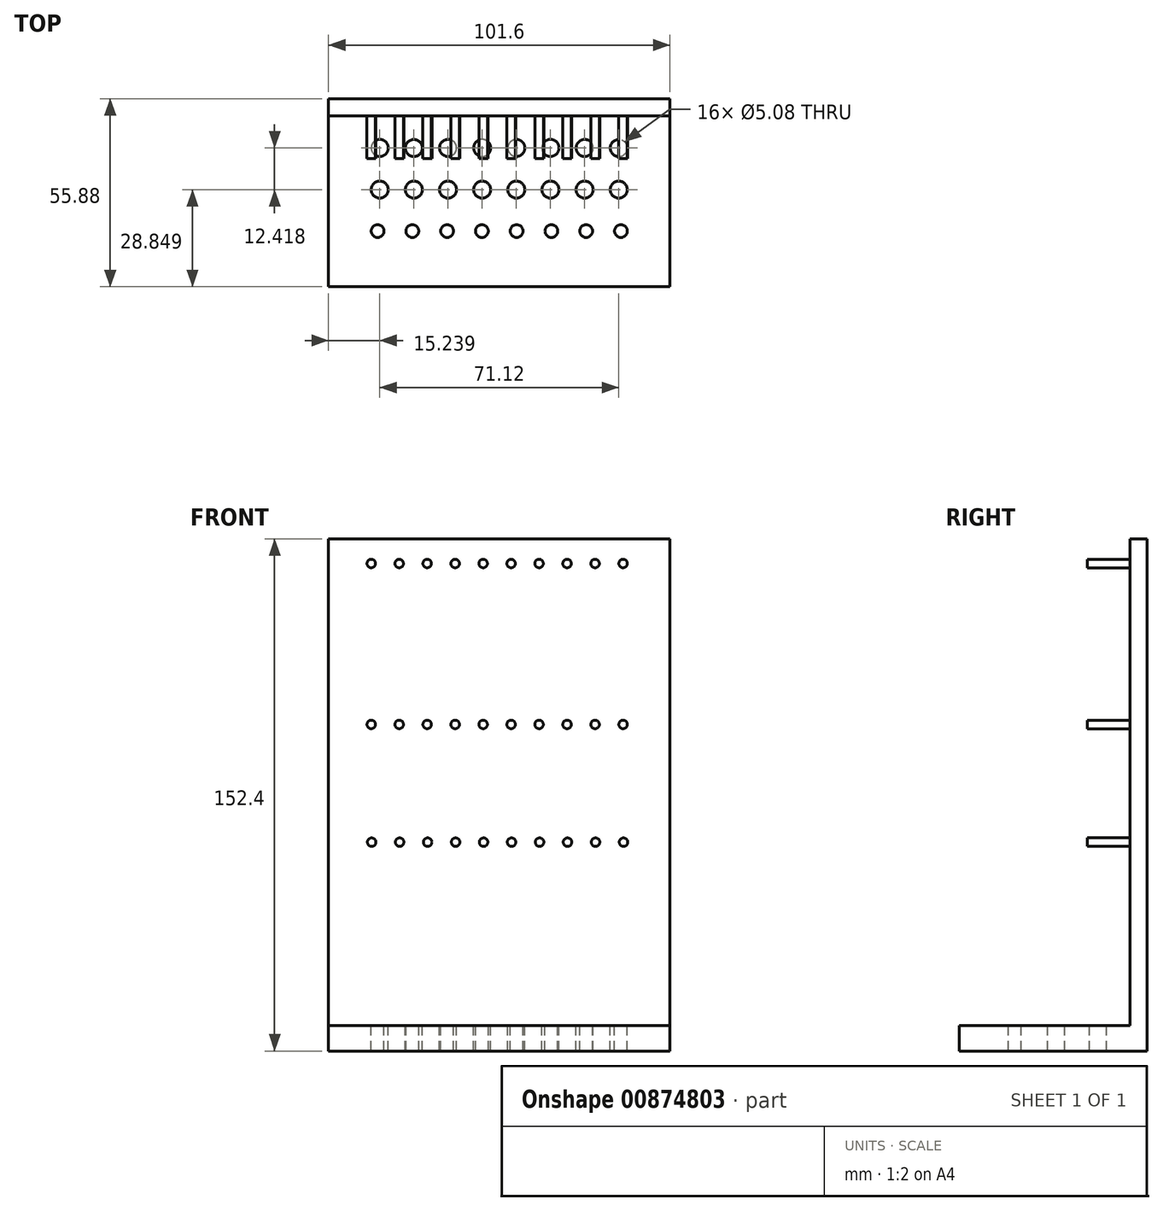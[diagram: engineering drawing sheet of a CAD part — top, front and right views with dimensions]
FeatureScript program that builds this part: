
annotation { "Feature Type Name" : "Feature", "Feature Type Description" : "" }
export const myFeature = defineFeature(function(context is Context, id is Id, definition is map)
    precondition{}
    {
        {
            var Q0;
            Q0=qCreatedBy(makeId("Front.planeOp"),FACE);
            var sketch = newSketch(context, id + "F0", { "sketchPlane" : qUnion([Q0])});
            skLineSegment(sketch, "E0", {"start": v(-60.63, 101.31) * mm, "end": v(40.97, 101.31) * mm});
            skLineSegment(sketch, "E1", {"start": v(40.97, 101.31) * mm, "end": v(40.97, -51.09) * mm});
            skLineSegment(sketch, "E2", {"start": v(40.97, -51.09) * mm, "end": v(-60.63, -51.09) * mm});
            skLineSegment(sketch, "E3", {"start": v(-60.63, -51.09) * mm, "end": v(-60.63, 101.31) * mm});
            skSolve(sketch);
        }
        {
            var Q0;
            Q0 = qSketchRegion(id + "F0", true);
            extrude(context, id + "F1", {"entities" : qUnion([Q0]), "depth" : 5.08 * mm, "offsetDistance" : 25.4 * mm});
        }
        {
            var Q0;
            Q0=makeQuery(id+"F1.opExtrude","CAP_FACE",FACE,{"disambiguationData":[OSD([sQuery(id+"F0.wireOp",EDGE,"E0"),sQuery(id+"F0.wireOp",EDGE,"E1"),sQuery(id+"F0.wireOp",EDGE,"E2"),sQuery(id+"F0.wireOp",EDGE,"E3")])],"isStart":false});
            var sketch = newSketch(context, id + "F2", { "sketchPlane" : qUnion([Q0])});
            skLineSegment(sketch, "E4", {"start": v(-60.63, -51.09) * mm, "end": v(40.97, -51.09) * mm});
            skLineSegment(sketch, "E5", {"start": v(40.97, -51.09) * mm, "end": v(40.97, -43.47) * mm});
            skLineSegment(sketch, "E6", {"start": v(40.97, -43.47) * mm, "end": v(-60.63, -43.47) * mm});
            skLineSegment(sketch, "E7", {"start": v(-60.63, -43.47) * mm, "end": v(-60.63, -51.09) * mm});
            skSolve(sketch);
        }
        {
            var Q0;
            Q0 = qSketchRegion(id + "F2", true);
            extrude(context, id + "F3", {"entities" : qUnion([Q0]), "operationType" : NewBodyOperationType.ADD, "depth" : 50.8 * mm, "offsetDistance" : 25.4 * mm});
        }
        {
            var Q0;
            Q0=makeQuery(id+"F3.opExtrude","SWEPT_FACE",FACE,{"disambiguationData":[OSD([sQuery(id+"F2.wireOp",EDGE,"E6")])]});
            var sketch = newSketch(context, id + "F4", { "sketchPlane" : qUnion([Q0])});
            skCircle(sketch, "E8", {"center": v(-45.4, -14.61) * mm, "radius": 2.54 * mm});
            skCircle(sketch, "E9.1.0.0", {"center": v(-35.23, -14.61) * mm, "radius": 2.54 * mm});
            skCircle(sketch, "E9.2.0.0", {"center": v(-25.07, -14.61) * mm, "radius": 2.54 * mm});
            skCircle(sketch, "E9.3.0.0", {"center": v(-14.91, -14.61) * mm, "radius": 2.54 * mm});
            skCircle(sketch, "E9.4.0.0", {"center": v(-4.75, -14.61) * mm, "radius": 2.54 * mm});
            skCircle(sketch, "E9.5.0.0", {"center": v(5.4, -14.61) * mm, "radius": 2.54 * mm});
            skCircle(sketch, "E9.6.0.0", {"center": v(15.57, -14.61) * mm, "radius": 2.54 * mm});
            skCircle(sketch, "E9.7.0.0", {"center": v(25.73, -14.61) * mm, "radius": 2.54 * mm});
            skLineSegment(sketch, "E9.direction1", {"start": v(-45.4, -14.61) * mm, "end": v(-35.23, -14.61) * mm, "construction": true});
            skSolve(sketch);
        }
        {
            var Q0;
            Q0 = qSketchRegion(id + "F4", true);
            extrude(context, id + "F5", {"entities" : qUnion([Q0]), "operationType" : NewBodyOperationType.REMOVE, "oppositeDirection" : true, "depth" : 25.4 * mm, "offsetDistance" : 25.4 * mm});
        }
        {
            var Q0;
            Q0=makeQuery(id+"F3.opExtrude","SWEPT_FACE",FACE,{"disambiguationData":[OSD([sQuery(id+"F2.wireOp",EDGE,"E6")])]});
            var sketch = newSketch(context, id + "F6", { "sketchPlane" : qUnion([Q0])});
            skCircle(sketch, "E10", {"center": v(-45.4, -27.03) * mm, "radius": 2.54 * mm});
            skCircle(sketch, "E11.1.0.0", {"center": v(-35.23, -27.03) * mm, "radius": 2.54 * mm});
            skCircle(sketch, "E11.2.0.0", {"center": v(-25.07, -27.03) * mm, "radius": 2.54 * mm});
            skCircle(sketch, "E11.3.0.0", {"center": v(-14.91, -27.03) * mm, "radius": 2.54 * mm});
            skCircle(sketch, "E11.4.0.0", {"center": v(-4.75, -27.03) * mm, "radius": 2.54 * mm});
            skCircle(sketch, "E11.5.0.0", {"center": v(5.4, -27.03) * mm, "radius": 2.54 * mm});
            skCircle(sketch, "E11.6.0.0", {"center": v(15.57, -27.03) * mm, "radius": 2.54 * mm});
            skCircle(sketch, "E11.7.0.0", {"center": v(25.73, -27.03) * mm, "radius": 2.54 * mm});
            skLineSegment(sketch, "E11.direction1", {"start": v(-45.4, -27.03) * mm, "end": v(-35.23, -27.03) * mm, "construction": true});
            skSolve(sketch);
        }
        {
            var Q0;
            Q0 = qSketchRegion(id + "F6", true);
            extrude(context, id + "F7", {"entities" : qUnion([Q0]), "operationType" : NewBodyOperationType.REMOVE, "oppositeDirection" : true, "depth" : 25.4 * mm, "offsetDistance" : 25.4 * mm});
        }
        {
            var Q0;
            Q0=makeQuery(id+"F3.opExtrude","SWEPT_FACE",FACE,{"disambiguationData":[OSD([sQuery(id+"F2.wireOp",EDGE,"E6")])]});
            var sketch = newSketch(context, id + "F8", { "sketchPlane" : qUnion([Q0])});
            skCircle(sketch, "E12", {"center": v(-46.03, -39.35) * mm, "radius": 1.9 * mm});
            skCircle(sketch, "E13.1.0.0", {"center": v(-35.68, -39.35) * mm, "radius": 1.9 * mm});
            skCircle(sketch, "E13.2.0.0", {"center": v(-25.34, -39.35) * mm, "radius": 1.9 * mm});
            skCircle(sketch, "E13.3.0.0", {"center": v(-15, -39.35) * mm, "radius": 1.9 * mm});
            skCircle(sketch, "E13.4.0.0", {"center": v(-4.66, -39.35) * mm, "radius": 1.9 * mm});
            skCircle(sketch, "E13.5.0.0", {"center": v(5.68, -39.35) * mm, "radius": 1.9 * mm});
            skCircle(sketch, "E13.6.0.0", {"center": v(16.02, -39.35) * mm, "radius": 1.9 * mm});
            skCircle(sketch, "E13.7.0.0", {"center": v(26.36, -39.35) * mm, "radius": 1.9 * mm});
            skLineSegment(sketch, "E13.direction1", {"start": v(-46.03, -39.35) * mm, "end": v(-35.68, -39.35) * mm, "construction": true});
            skSolve(sketch);
        }
        {
            var Q0;
            Q0=makeQuery(id+"F8.imprint","IMPRINT",FACE,{"disambiguationData":[TD([[makeQuery(id+"F8.imprint","IMPRINT",EDGE,{"derivedFrom":sQuery(id+"F8.wireOp",EDGE,"E13.7.0.0")}),1.0]])]});
            var Q1;
            Q1=makeQuery(id+"F8.imprint","IMPRINT",FACE,{"disambiguationData":[TD([[makeQuery(id+"F8.imprint","IMPRINT",EDGE,{"derivedFrom":sQuery(id+"F8.wireOp",EDGE,"E13.6.0.0")}),1.0]])]});
            var Q2;
            Q2=makeQuery(id+"F8.imprint","IMPRINT",FACE,{"disambiguationData":[TD([[makeQuery(id+"F8.imprint","IMPRINT",EDGE,{"derivedFrom":sQuery(id+"F8.wireOp",EDGE,"E13.5.0.0")}),1.0]])]});
            var Q3;
            Q3=makeQuery(id+"F8.imprint","IMPRINT",FACE,{"disambiguationData":[TD([[makeQuery(id+"F8.imprint","IMPRINT",EDGE,{"derivedFrom":sQuery(id+"F8.wireOp",EDGE,"E13.4.0.0")}),1.0]])]});
            var Q4;
            Q4=makeQuery(id+"F8.imprint","IMPRINT",FACE,{"disambiguationData":[TD([[makeQuery(id+"F8.imprint","IMPRINT",EDGE,{"derivedFrom":sQuery(id+"F8.wireOp",EDGE,"E13.3.0.0")}),1.0]])]});
            var Q5;
            Q5=makeQuery(id+"F8.imprint","IMPRINT",FACE,{"disambiguationData":[TD([[makeQuery(id+"F8.imprint","IMPRINT",EDGE,{"derivedFrom":sQuery(id+"F8.wireOp",EDGE,"E13.2.0.0")}),1.0]])]});
            var Q6;
            Q6=makeQuery(id+"F8.imprint","IMPRINT",FACE,{"disambiguationData":[TD([[makeQuery(id+"F8.imprint","IMPRINT",EDGE,{"derivedFrom":sQuery(id+"F8.wireOp",EDGE,"E13.1.0.0")}),1.0]])]});
            var Q7;
            Q7=makeQuery(id+"F8.imprint","IMPRINT",FACE,{"disambiguationData":[TD([[makeQuery(id+"F8.imprint","IMPRINT",EDGE,{"derivedFrom":sQuery(id+"F8.wireOp",EDGE,"E12")}),1.0]])]});
            extrude(context, id + "F9", {"entities" : qUnion([Q0, Q1, Q2, Q3, Q4, Q5, Q6, Q7]), "operationType" : NewBodyOperationType.REMOVE, "oppositeDirection" : true, "depth" : 25.4 * mm, "offsetDistance" : 25.4 * mm});
        }
        {
            var Q0;
            Q0=makeQuery(id+"F1.opExtrude","CAP_FACE",FACE,{"disambiguationData":[OSD([sQuery(id+"F0.wireOp",EDGE,"E0"),sQuery(id+"F0.wireOp",EDGE,"E1"),sQuery(id+"F0.wireOp",EDGE,"E2"),sQuery(id+"F0.wireOp",EDGE,"E3")])],"isStart":false});
            var sketch = newSketch(context, id + "F10", { "sketchPlane" : qUnion([Q0])});
            skCircle(sketch, "E14", {"center": v(-47.93, 93.94) * mm, "radius": 1.27 * mm});
            skCircle(sketch, "E15.1.0.0", {"center": v(-39.6, 93.94) * mm, "radius": 1.27 * mm});
            skCircle(sketch, "E15.2.0.0", {"center": v(-31.28, 93.94) * mm, "radius": 1.27 * mm});
            skCircle(sketch, "E15.3.0.0", {"center": v(-22.95, 93.94) * mm, "radius": 1.27 * mm});
            skCircle(sketch, "E15.4.0.0", {"center": v(-14.63, 93.94) * mm, "radius": 1.27 * mm});
            skCircle(sketch, "E15.5.0.0", {"center": v(-6.3, 93.94) * mm, "radius": 1.27 * mm});
            skCircle(sketch, "E15.6.0.0", {"center": v(2.02, 93.94) * mm, "radius": 1.27 * mm});
            skCircle(sketch, "E15.7.0.0", {"center": v(10.35, 93.94) * mm, "radius": 1.27 * mm});
            skCircle(sketch, "E15.8.0.0", {"center": v(18.67, 93.94) * mm, "radius": 1.27 * mm});
            skCircle(sketch, "E15.9.0.0", {"center": v(27, 93.94) * mm, "radius": 1.27 * mm});
            skLineSegment(sketch, "E15.direction1", {"start": v(-47.93, 93.94) * mm, "end": v(-39.6, 93.94) * mm, "construction": true});
            skSolve(sketch);
        }
        {
            var Q0;
            Q0 = qSketchRegion(id + "F10", true);
            extrude(context, id + "F11", {"entities" : qUnion([Q0]), "operationType" : NewBodyOperationType.ADD, "depth" : 12.7 * mm, "offsetDistance" : 25.4 * mm});
        }
        {
            var Q0;
            Q0=makeQuery(id+"F1.opExtrude","CAP_FACE",FACE,{"disambiguationData":[OSD([sQuery(id+"F0.wireOp",EDGE,"E0"),sQuery(id+"F0.wireOp",EDGE,"E1"),sQuery(id+"F0.wireOp",EDGE,"E2"),sQuery(id+"F0.wireOp",EDGE,"E3")])],"isStart":false});
            var sketch = newSketch(context, id + "F12", { "sketchPlane" : qUnion([Q0])});
            skCircle(sketch, "E16", {"center": v(-47.93, 46.07) * mm, "radius": 1.27 * mm});
            skCircle(sketch, "E17.1.0.0", {"center": v(-39.6, 46.07) * mm, "radius": 1.27 * mm});
            skCircle(sketch, "E17.2.0.0", {"center": v(-31.28, 46.07) * mm, "radius": 1.27 * mm});
            skCircle(sketch, "E17.3.0.0", {"center": v(-22.95, 46.07) * mm, "radius": 1.27 * mm});
            skCircle(sketch, "E17.4.0.0", {"center": v(-14.63, 46.07) * mm, "radius": 1.27 * mm});
            skCircle(sketch, "E17.5.0.0", {"center": v(-6.3, 46.07) * mm, "radius": 1.27 * mm});
            skCircle(sketch, "E17.6.0.0", {"center": v(2.02, 46.07) * mm, "radius": 1.27 * mm});
            skCircle(sketch, "E17.7.0.0", {"center": v(10.35, 46.07) * mm, "radius": 1.27 * mm});
            skCircle(sketch, "E17.8.0.0", {"center": v(18.67, 46.07) * mm, "radius": 1.27 * mm});
            skCircle(sketch, "E17.9.0.0", {"center": v(27, 46.07) * mm, "radius": 1.27 * mm});
            skLineSegment(sketch, "E17.direction1", {"start": v(-47.93, 46.07) * mm, "end": v(-39.6, 46.07) * mm, "construction": true});
            skSolve(sketch);
        }
        {
            var Q0;
            Q0 = qSketchRegion(id + "F12", true);
            extrude(context, id + "F13", {"entities" : qUnion([Q0]), "operationType" : NewBodyOperationType.ADD, "depth" : 12.7 * mm, "offsetDistance" : 25.4 * mm});
        }
        {
            var Q0;
            Q0=makeQuery(id+"F1.opExtrude","CAP_FACE",FACE,{"disambiguationData":[OSD([sQuery(id+"F0.wireOp",EDGE,"E0"),sQuery(id+"F0.wireOp",EDGE,"E1"),sQuery(id+"F0.wireOp",EDGE,"E2"),sQuery(id+"F0.wireOp",EDGE,"E3")])],"isStart":false});
            var sketch = newSketch(context, id + "F14", { "sketchPlane" : qUnion([Q0])});
            skCircle(sketch, "E18", {"center": v(-47.8, 11.04) * mm, "radius": 1.27 * mm});
            skCircle(sketch, "E19.1.0.0", {"center": v(-39.47, 11.04) * mm, "radius": 1.27 * mm});
            skCircle(sketch, "E19.2.0.0", {"center": v(-31.14, 11.04) * mm, "radius": 1.27 * mm});
            skCircle(sketch, "E19.3.0.0", {"center": v(-22.81, 11.04) * mm, "radius": 1.27 * mm});
            skCircle(sketch, "E19.4.0.0", {"center": v(-14.49, 11.04) * mm, "radius": 1.27 * mm});
            skCircle(sketch, "E19.5.0.0", {"center": v(-6.16, 11.04) * mm, "radius": 1.27 * mm});
            skCircle(sketch, "E19.6.0.0", {"center": v(2.16, 11.04) * mm, "radius": 1.27 * mm});
            skCircle(sketch, "E19.7.0.0", {"center": v(10.49, 11.04) * mm, "radius": 1.27 * mm});
            skCircle(sketch, "E19.8.0.0", {"center": v(18.81, 11.04) * mm, "radius": 1.27 * mm});
            skCircle(sketch, "E19.9.0.0", {"center": v(27.14, 11.04) * mm, "radius": 1.27 * mm});
            skLineSegment(sketch, "E19.direction1", {"start": v(-47.8, 11.04) * mm, "end": v(-39.47, 11.04) * mm, "construction": true});
            skSolve(sketch);
        }
        {
            var Q0;
            Q0 = qSketchRegion(id + "F14", true);
            extrude(context, id + "F15", {"entities" : qUnion([Q0]), "operationType" : NewBodyOperationType.ADD, "depth" : 12.7 * mm, "offsetDistance" : 25.4 * mm});
        }
    });
